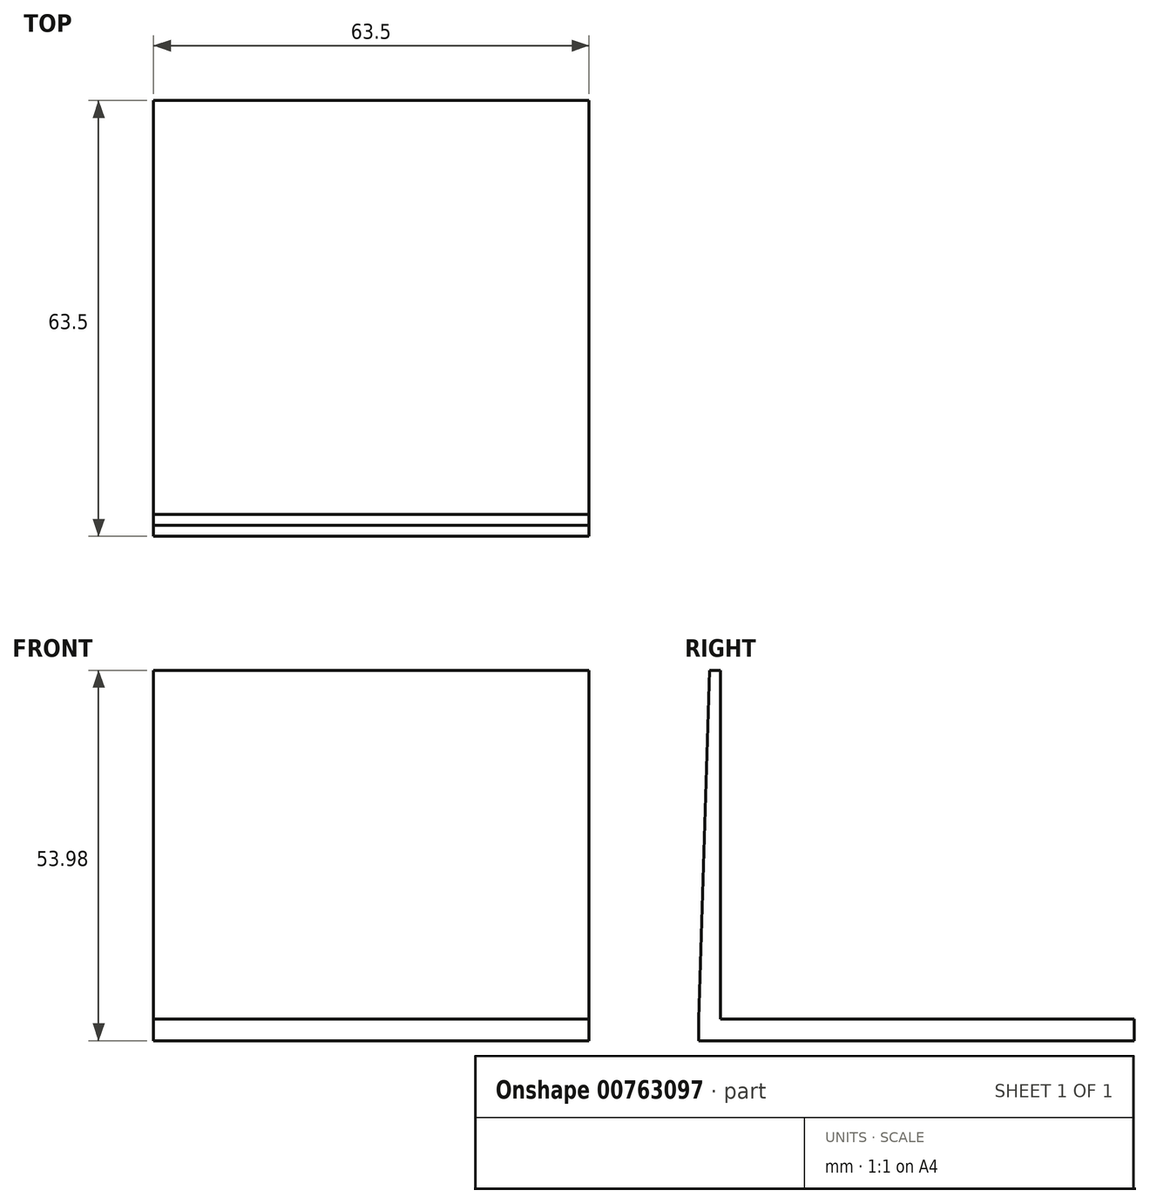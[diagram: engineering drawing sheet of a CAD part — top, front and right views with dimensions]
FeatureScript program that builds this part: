
annotation { "Feature Type Name" : "Feature", "Feature Type Description" : "" }
export const myFeature = defineFeature(function(context is Context, id is Id, definition is map)
    precondition{}
    {
        {
            var Q0;
            Q0=qCreatedBy(makeId("Top.planeOp"),FACE);
            var sketch = newSketch(context, id + "F0", { "sketchPlane" : qUnion([Q0])});
            skLineSegment(sketch, "E0.bottom", {"start": v(0, 0) * mm, "end": v(-63.5, 0) * mm});
            skLineSegment(sketch, "E0.top", {"start": v(0, -63.5) * mm, "end": v(-63.5, -63.5) * mm});
            skLineSegment(sketch, "E0.left", {"start": v(0, 0) * mm, "end": v(0, -63.5) * mm});
            skLineSegment(sketch, "E0.right", {"start": v(-63.5, 0) * mm, "end": v(-63.5, -63.5) * mm});
            skSolve(sketch);
        }
        {
            var Q0;
            Q0 = qSketchRegion(id + "F0", true);
            extrude(context, id + "F1", {"entities" : qUnion([Q0]), "depth" : 3.17 * mm, "offsetDistance" : 25.4 * mm});
        }
        {
            var Q0;
            Q0=makeQuery(id+"F1.opExtrude","CAP_FACE",FACE,{"disambiguationData":[OSD([sQuery(id+"F0.wireOp",EDGE,"E0.bottom"),sQuery(id+"F0.wireOp",EDGE,"E0.top"),sQuery(id+"F0.wireOp",EDGE,"E0.left"),sQuery(id+"F0.wireOp",EDGE,"E0.right")])],"isStart":false});
            var sketch = newSketch(context, id + "F2", { "sketchPlane" : qUnion([Q0])});
            skLineSegment(sketch, "E1.bottom", {"start": v(0, -63.5) * mm, "end": v(-63.5, -63.5) * mm});
            skLineSegment(sketch, "E1.top", {"start": v(0, -60.33) * mm, "end": v(-63.5, -60.33) * mm});
            skLineSegment(sketch, "E1.left", {"start": v(0, -63.5) * mm, "end": v(0, -60.33) * mm});
            skLineSegment(sketch, "E1.right", {"start": v(-63.5, -63.5) * mm, "end": v(-63.5, -60.33) * mm});
            skSolve(sketch);
        }
        {
            var Q0;
            Q0 = qSketchRegion(id + "F2", true);
            extrude(context, id + "F3", {"entities" : qUnion([Q0]), "operationType" : NewBodyOperationType.ADD, "depth" : 50.8 * mm, "offsetDistance" : 25.4 * mm});
        }
        {
            var Q0;
            Q0=makeQuery(id+"F3.boolean.opBoolean","MERGE",FACE,{"derivedFrom":[makeQuery(id+"F1.opExtrude","SWEPT_FACE",FACE,{"disambiguationData":[OSD([sQuery(id+"F0.wireOp",EDGE,"E0.right")])]}),makeQuery(id+"F3.opExtrude","SWEPT_FACE",FACE,{"disambiguationData":[OSD([sQuery(id+"F2.wireOp",EDGE,"E1.right")])]})]});
            var sketch = newSketch(context, id + "F4", { "sketchPlane" : qUnion([Q0])});
            skLineSegment(sketch, "E2", {"start": v(63.5, 3.18) * mm, "end": v(61.91, 53.98) * mm});
            skLineSegment(sketch, "E3", {"start": v(61.91, 53.98) * mm, "end": v(60.32, 53.98) * mm});
            skLineSegment(sketch, "E4", {"start": v(60.32, 53.98) * mm, "end": v(60.32, 3.18) * mm});
            skLineSegment(sketch, "E5", {"start": v(60.32, 3.18) * mm, "end": v(63.5, 3.18) * mm});
            skSolve(sketch);
        }
        {
            var Q0;
            {var subQ0=sQuery(id+"F4.wireOp",EDGE,"E2");Q0=makeQuery(id+"F4.imprint","IMPRINT",FACE,{"disambiguationData":[TD([[makeQuery(id+"F4.imprint","IMPRINT",EDGE,{"derivedFrom":subQ0}),-1.0]])]});}
            extrude(context, id + "F5", {"entities" : qUnion([Q0]), "operationType" : NewBodyOperationType.REMOVE, "oppositeDirection" : true, "depth" : 63.5 * mm, "offsetDistance" : 25.4 * mm});
        }
    });
